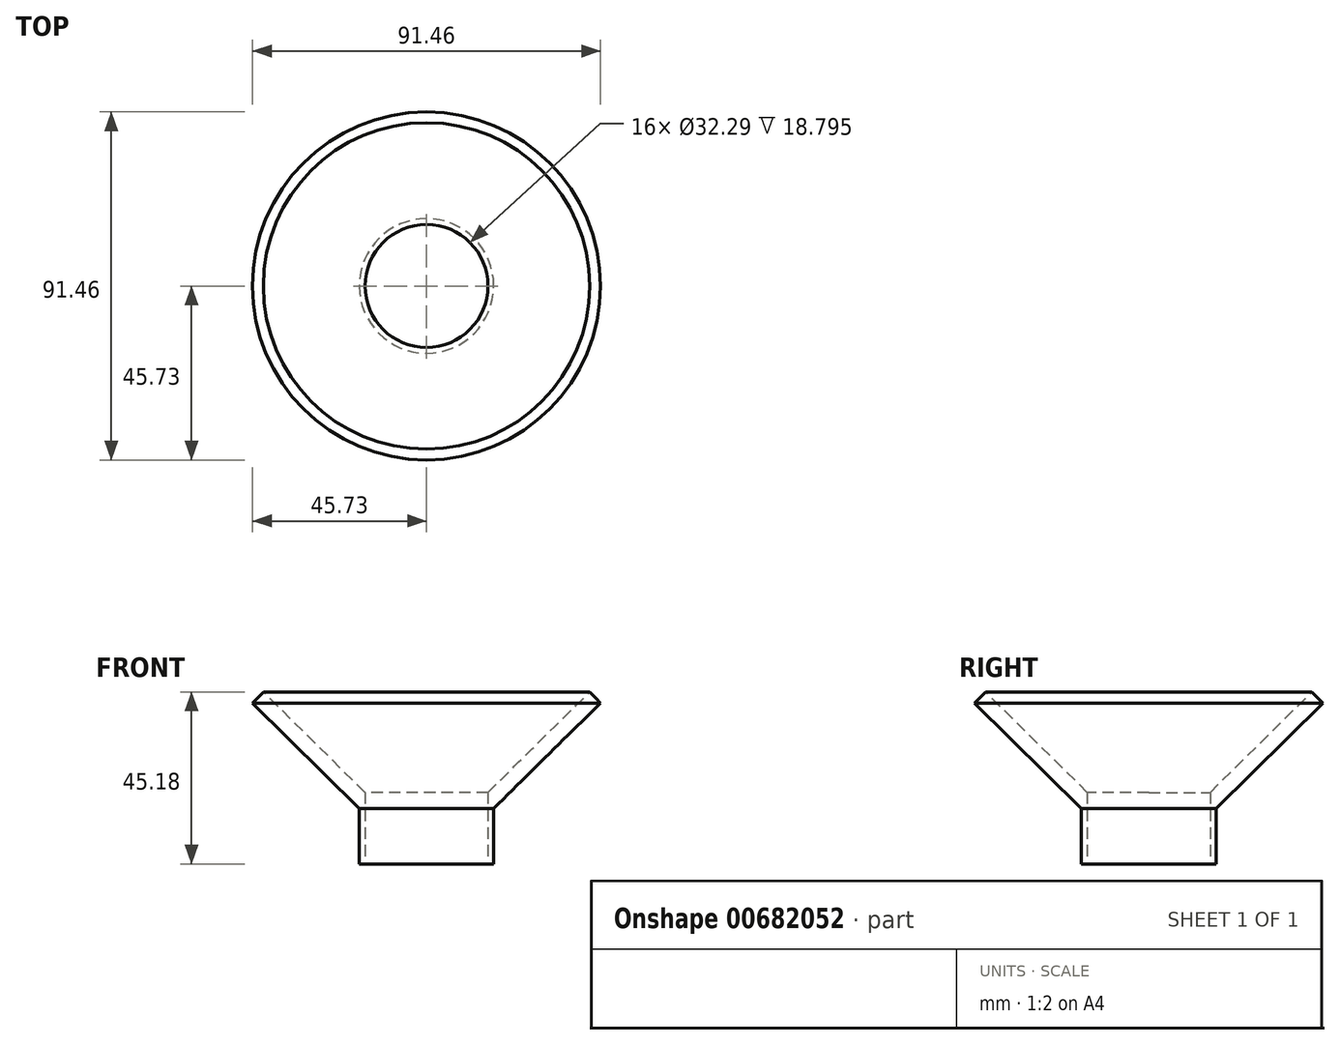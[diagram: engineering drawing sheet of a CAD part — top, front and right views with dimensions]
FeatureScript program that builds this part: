
annotation { "Feature Type Name" : "Feature", "Feature Type Description" : "" }
export const myFeature = defineFeature(function(context is Context, id is Id, definition is map)
    precondition{}
    {
        {
            var Q0;
            Q0=qCreatedBy(makeId("Front.planeOp"),FACE);
            var sketch = newSketch(context, id + "F0", { "sketchPlane" : qUnion([Q0])});
            skLineSegment(sketch, "E0", {"start": v(0, 0) * mm, "end": v(17.66, 0) * mm});
            skLineSegment(sketch, "E1", {"start": v(17.66, 0) * mm, "end": v(17.66, 14.6) * mm});
            skLineSegment(sketch, "E2", {"start": v(17.66, 14.6) * mm, "end": v(45.73, 42.3) * mm});
            skLineSegment(sketch, "E3", {"start": v(45.73, 42.3) * mm, "end": v(42.9, 45.18) * mm});
            skLineSegment(sketch, "E4", {"start": v(42.9, 45.18) * mm, "end": v(15.76, 18.42) * mm});
            skLineSegment(sketch, "E5", {"start": v(15.76, 18.42) * mm, "end": v(0, 18.42) * mm});
            skLineSegment(sketch, "E6", {"start": v(0, 18.42) * mm, "end": v(0, 0) * mm});
            skSolve(sketch);
        }
        {
            var Q0;
            Q0=makeQuery(id+"F0.imprint","IMPRINT",FACE,{"disambiguationData":[TD([[makeQuery(id+"F0.imprint","IMPRINT",EDGE,{"derivedFrom":sQuery(id+"F0.wireOp",EDGE,"E0")}),1.0]])]});
            var Q1;
            Q1=sQuery(id+"F0.wireOp",EDGE,"E6");
            revolve(context, id + "F1", {"surfaceOperationType" : NewSurfaceOperationType.NEW, "entities" : qUnion([Q0]), "axis" : qUnion([Q1]), "revolveType" : RevolveType.FULL});
        }
        {
            var Q0;
            Q0=makeQuery(id+"F1.opRevolve","SWEPT_FACE",FACE,{"disambiguationData":[OSD([sQuery(id+"F0.wireOp",EDGE,"E0")])]});
            var sketch = newSketch(context, id + "F2", { "sketchPlane" : qUnion([Q0])});
            skCircle(sketch, "E7", {"center": v(0, 0) * mm, "radius": 16.14 * mm});
            skSolve(sketch);
        }
        {
            var Q0;
            Q0 = qSketchRegion(id + "F2", true);
            extrude(context, id + "F3", {"entities" : qUnion([Q0]), "operationType" : NewBodyOperationType.REMOVE, "oppositeDirection" : true, "depth" : 25.4 * mm, "offsetDistance" : 25.4 * mm});
        }
    });
